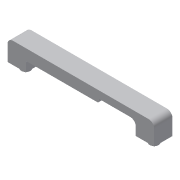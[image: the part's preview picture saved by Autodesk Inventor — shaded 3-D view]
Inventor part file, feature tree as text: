
AUTODESK INVENTOR PART (.ipt)
format: ipt  version: 2013 (Build 170138000, 138)  size: 124,416 bytes
history: native  units: mm
features: extrude x5, sketch x5, fillet x2, projected_geometry x1
ambient origin geometry x8: Origin, YZ Plane, XZ Plane, XY Plane, X Axis, Y Axis, Z Axis, Center Point
bodies: Volumenkörper1 (feature_tree)
feature tree (13):
  extrude  "Extrusion1"  Depth=10.0mm
  extrude  "Extrusion2"  Depth=10.0mm
  fillet  "Rundung1"  Radius=60.0mm
  extrude  "Extrusion3"  Depth=4.0mm TaperAngle=0.0deg
  fillet  "Rundung2"  Radius=3.0mm
  sketch  "Skizze4"  dims[d10=3.0mm d11=3.0mm]
  sketch  "Skizze5"  dims[d12=3.0mm d13=50.0mm d14=2.0mm d15=2.0mm d16=0.0mm d17=1.0mm d18=5.0mm d19=5.0mm d20=5.0mm d21=5.0mm d22=5.0mm d23=5.0mm d24=3.0mm d25=0.0mm d26=3.0mm d27=0.0mm]
  extrude  "Extrusion4"  Depth=3.0mm
  extrude  "Extrusion5"  Depth=50.0mm
  sketch  "Skizze1"  dims[d0=10.0mm d1=10.0mm]
  sketch  "Skizze2"  dims[d2=10.0mm d3=10.0mm d4=60.0mm]
  projected_geometry  "Projizierte Kontur1"
  sketch  "Skizze3"  dims[d5=7.5mm d6=0.0mm d7=4.0mm d8=0.0mm d9=3.0mm]
